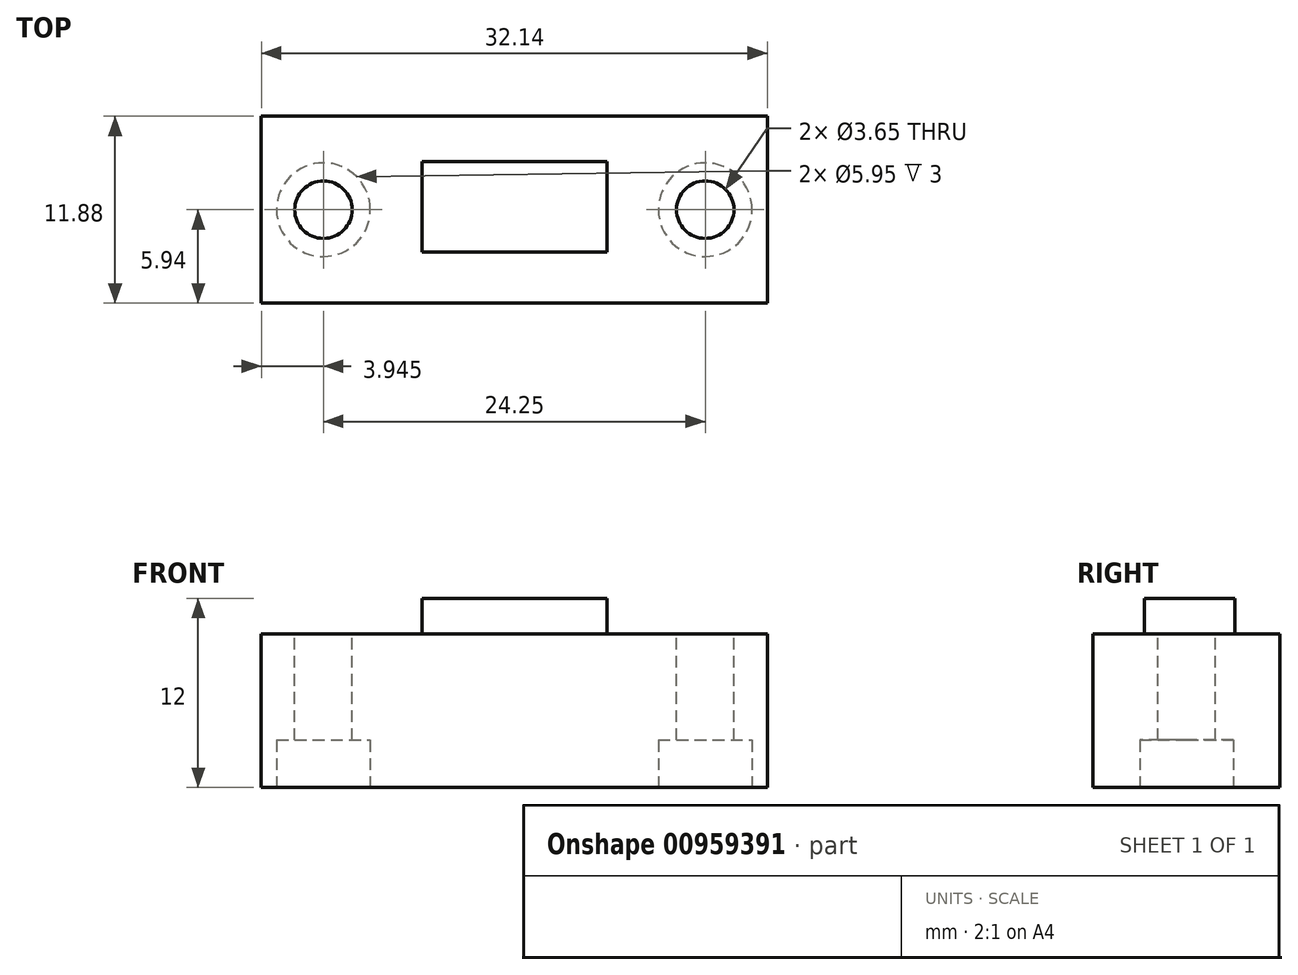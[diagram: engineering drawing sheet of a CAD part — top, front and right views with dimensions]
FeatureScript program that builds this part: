
annotation { "Feature Type Name" : "Feature", "Feature Type Description" : "" }
export const myFeature = defineFeature(function(context is Context, id is Id, definition is map)
    precondition{}
    {
        {
            assignVariable(context, id + "F0", {"name" : "tolerance", "anyValue" : 0.25});
        }
        {
            var Q0;
            Q0=qCreatedBy(makeId("Top.planeOp"),FACE);
            var sketch = newSketch(context, id + "F1", { "sketchPlane" : qUnion([Q0])});
            skLineSegment(sketch, "E0.bottom", {"start": v(16.07, 5.94) * mm, "end": v(-16.07, 5.94) * mm});
            skLineSegment(sketch, "E0.top", {"start": v(16.07, -5.94) * mm, "end": v(-16.07, -5.94) * mm});
            skLineSegment(sketch, "E0.left", {"start": v(16.07, 5.94) * mm, "end": v(16.07, -5.94) * mm});
            skLineSegment(sketch, "E0.right", {"start": v(-16.07, 5.94) * mm, "end": v(-16.07, -5.94) * mm});
            skPoint(sketch, "E0.middle", {"position": v(0, 0) * mm});
            skLineSegment(sketch, "E1.bottom", {"start": v(5.87, 3.06) * mm, "end": v(0, 3.06) * mm});
            skLineSegment(sketch, "E1.top", {"start": v(5.88, -2.69) * mm, "end": v(0, -2.69) * mm});
            skLineSegment(sketch, "E1.left", {"start": v(5.88, 3.06) * mm, "end": v(5.88, -2.69) * mm});
            skLineSegment(sketch, "E1.right", {"start": v(0, 3.06) * mm, "end": v(0, -2.69) * mm});
            skLineSegment(sketch, "E2.bottom", {"start": v(7.88, 5.94) * mm, "end": v(0, 5.94) * mm});
            skLineSegment(sketch, "E2.top", {"start": v(7.88, 3.06) * mm, "end": v(0, 3.06) * mm});
            skLineSegment(sketch, "E2.left", {"start": v(7.88, 5.94) * mm, "end": v(7.88, 3.06) * mm});
            skLineSegment(sketch, "E2.right", {"start": v(0, 5.94) * mm, "end": v(0, 3.06) * mm});
            skLineSegment(sketch, "E3.bottom", {"start": v(7.88, -5.94) * mm, "end": v(0, -5.94) * mm});
            skLineSegment(sketch, "E3.top", {"start": v(7.88, -2.69) * mm, "end": v(0, -2.69) * mm});
            skLineSegment(sketch, "E3.left", {"start": v(7.88, -5.94) * mm, "end": v(7.88, -2.69) * mm});
            skLineSegment(sketch, "E3.right", {"start": v(0, -5.94) * mm, "end": v(0, -2.69) * mm});
            skCircle(sketch, "E4", {"center": v(12.12, 0) * mm, "radius": 1.82 * mm});
            skCircle(sketch, "E5", {"center": v(-12.12, 0) * mm, "radius": 1.83 * mm});
            skLineSegment(sketch, "E6.MirrorCS", {"start": v(-7.88, 5.94) * mm, "end": v(-7.88, 3.06) * mm});
            skLineSegment(sketch, "E7.MirrorCS", {"start": v(-5.87, 3.06) * mm, "end": v(0, 3.06) * mm});
            skLineSegment(sketch, "E8.MirrorCS", {"start": v(-7.88, 3.06) * mm, "end": v(0, 3.06) * mm});
            skLineSegment(sketch, "E9.MirrorCS", {"start": v(-5.88, 3.06) * mm, "end": v(-5.88, -2.69) * mm});
            skLineSegment(sketch, "E10.MirrorCS", {"start": v(-7.88, -2.69) * mm, "end": v(0, -2.69) * mm});
            skLineSegment(sketch, "E11.MirrorCS", {"start": v(-7.88, -5.94) * mm, "end": v(-7.88, -2.69) * mm});
            skSolve(sketch);
        }
        {
            var Q0;
            {var subQ0=sQuery(id+"F1.wireOp",EDGE,"E0.right");Q0=makeQuery(id+"F1.imprint","IMPRINT",FACE,{"disambiguationData":[TD([[makeQuery(id+"F1.imprint","IMPRINT",EDGE,{"derivedFrom":subQ0}),1.0]])]});}
            var Q1;
            {var subQ0=sQuery(id+"F1.wireOp",EDGE,"E1.right");Q1=makeQuery(id+"F1.imprint","IMPRINT",FACE,{"disambiguationData":[TD([[makeQuery(id+"F1.imprint","IMPRINT",EDGE,{"derivedFrom":subQ0}),-1.0]])]});}
            var Q2;
            {var subQ3=sQuery(id+"F1.wireOp",EDGE,"E3.right");Q2=makeQuery(id+"F1.imprint","IMPRINT",FACE,{"disambiguationData":[TD([[makeQuery(id+"F1.imprint","IMPRINT",EDGE,{"derivedFrom":subQ3}),1.0]])]});}
            var Q3;
            Q3=makeQuery(id+"F1.imprint","IMPRINT",FACE,{"disambiguationData":[TD([[makeQuery(id+"F1.imprint","IMPRINT",EDGE,{"derivedFrom":sQuery(id+"F1.wireOp",EDGE,"E1.top")}),1.0]])]});
            var Q4;
            {var subQ1=sQuery(id+"F1.wireOp",EDGE,"E2.right");Q4=makeQuery(id+"F1.imprint","IMPRINT",FACE,{"disambiguationData":[TD([[makeQuery(id+"F1.imprint","IMPRINT",EDGE,{"derivedFrom":subQ1}),-1.0]])]});}
            var Q5;
            Q5=makeQuery(id+"F1.imprint","IMPRINT",FACE,{"disambiguationData":[TD([[makeQuery(id+"F1.imprint","IMPRINT",EDGE,{"derivedFrom":sQuery(id+"F1.wireOp",EDGE,"E1.bottom")}),-1.0]])]});
            var Q6;
            Q6=makeQuery(id+"F1.imprint","IMPRINT",FACE,{"disambiguationData":[TD([[makeQuery(id+"F1.imprint","IMPRINT",EDGE,{"derivedFrom":sQuery(id+"F1.wireOp",EDGE,"E1.bottom")}),1.0]])]});
            var Q7;
            {var subQ0=sQuery(id+"F1.wireOp",EDGE,"E0.left");Q7=makeQuery(id+"F1.imprint","IMPRINT",FACE,{"disambiguationData":[TD([[makeQuery(id+"F1.imprint","IMPRINT",EDGE,{"derivedFrom":subQ0}),-1.0]])]});}
            extrude(context, id + "F2", {"entities" : qUnion([Q0, Q1, Q2, Q3, Q4, Q5, Q6, Q7]), "oppositeDirection" : true, "depth" : (10 - getVariable(context, 'tolerance')) * mm, "offsetDistance" : 25 * mm});
        }
        {
            var Q0;
            {var subQ0=sQuery(id+"F1.wireOp",EDGE,"E1.right");Q0=makeQuery(id+"F1.imprint","IMPRINT",FACE,{"disambiguationData":[TD([[makeQuery(id+"F1.imprint","IMPRINT",EDGE,{"derivedFrom":subQ0}),-1.0]])]});}
            var Q1;
            Q1=makeQuery(id+"F1.imprint","IMPRINT",FACE,{"disambiguationData":[TD([[makeQuery(id+"F1.imprint","IMPRINT",EDGE,{"derivedFrom":sQuery(id+"F1.wireOp",EDGE,"E1.bottom")}),1.0]])]});
            extrude(context, id + "F3", {"entities" : qUnion([Q0, Q1]), "operationType" : NewBodyOperationType.ADD, "depth" : (8 - (12 / 2) + getVariable(context, 'tolerance')) * mm, "offsetDistance" : 25 * mm});
        }
        {
            var Q0;
            Q0=makeQuery(id+"F2.opExtrude","CAP_FACE",FACE,{"disambiguationData":[OSD([sQuery(id+"F1.wireOp",EDGE,"E0.bottom"),sQuery(id+"F1.wireOp",EDGE,"E0.top"),sQuery(id+"F1.wireOp",EDGE,"E0.left"),sQuery(id+"F1.wireOp",EDGE,"E0.right"),sQuery(id+"F1.wireOp",EDGE,"E4"),sQuery(id+"F1.wireOp",EDGE,"E5")])],"isStart":false});
            var sketch = newSketch(context, id + "F4", { "sketchPlane" : qUnion([Q0])});
            skCircle(sketch, "E12.0", {"center": v(12.12, 0) * mm, "radius": 1.82 * mm});
            skCircle(sketch, "E12.1", {"center": v(-12.12, 0) * mm, "radius": 1.83 * mm});
            skCircle(sketch, "E13", {"center": v(12.12, 0) * mm, "radius": 2.98 * mm});
            skCircle(sketch, "E14", {"center": v(-12.12, 0) * mm, "radius": 2.98 * mm});
            skSolve(sketch);
        }
        {
            var Q0;
            Q0=makeQuery(id+"F4.imprint","IMPRINT",FACE,{"disambiguationData":[TD([[makeQuery(id+"F4.imprint","IMPRINT",EDGE,{"derivedFrom":sQuery(id+"F4.wireOp",EDGE,"E12.0")}),-1.0]])]});
            var Q1;
            Q1=makeQuery(id+"F4.imprint","IMPRINT",FACE,{"disambiguationData":[TD([[makeQuery(id+"F4.imprint","IMPRINT",EDGE,{"derivedFrom":sQuery(id+"F4.wireOp",EDGE,"E12.1")}),-1.0]])]});
            var Q2;
            Q2=makeQuery(id+"F4.imprint","IMPRINT",FACE,{"disambiguationData":[TD([[makeQuery(id+"F4.imprint","IMPRINT",EDGE,{"derivedFrom":sQuery(id+"F4.wireOp",EDGE,"E12.0")}),1.0]])]});
            var Q3;
            Q3=makeQuery(id+"F4.imprint","IMPRINT",FACE,{"disambiguationData":[TD([[makeQuery(id+"F4.imprint","IMPRINT",EDGE,{"derivedFrom":sQuery(id+"F4.wireOp",EDGE,"E12.1")}),1.0]])]});
            extrude(context, id + "F5", {"entities" : qUnion([Q0, Q1, Q2, Q3]), "operationType" : NewBodyOperationType.REMOVE, "oppositeDirection" : true, "depth" : 3 * mm, "offsetDistance" : 25 * mm});
        }
    });
